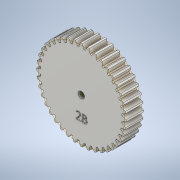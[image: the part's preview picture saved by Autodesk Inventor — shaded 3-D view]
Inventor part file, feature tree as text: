
AUTODESK INVENTOR PART (.ipt)
format: ipt  version: 2021 (Build 250183000, 183)  size: 401,408 bytes
history: native  units: mm (DEFAULTED — no unit token found)
features: sketch x5, plane x3, other x3, extrude x1, hole x1, emboss x1
ambient origin geometry x8: Origin, YZ Plane, XZ Plane, XY Plane, X Axis, Y Axis, Z Axis, Center Point
bodies: Solid1 (feature_tree)
feature tree (14):
  extrude  "Extrusion1"  Depth=8.0mm TaperAngle=0.0deg
  plane  "Work Plane2"
  plane  "Work Plane8"
  plane  "Work Plane9"
  other  "Spur Gear"
  sketch  "Sketch3"  dims[d16=25.351695mm]
  hole  "Hole1"  [1 undecoded]
  emboss  "Emboss1"
  sketch  "Sketch1"  dims[d0=41.564361mm d1=8.0mm d2=0.0mm]
  sketch  "Sketch2"  dims[d3=40.0mm d4=10.0mm d5=0.0mm]
  other  "Srf1"
  sketch  "Sketch4"  dims[d17=0.0mm d34=0.785398mm]
  sketch  "Sketch5"  dims[d39=0.0mm d41=0.0mm d43=25.351695mm d46=25.351695mm d47=0.0mm d48=0.0mm d49=3.0mm d50=3.0mm d51=6.0mm d52=4.0mm d53=2.0mm d54=90.0deg d55=8.0mm d56=20.594885mm d57=1.0mm d58=0.0mm]
  other  "Pitch Diameter"
note: 1 required parameter value undecoded (feature->parameter linkage not recoverable at this tier; creation-order binding heuristic only, values carry confidence <= 0.55)
